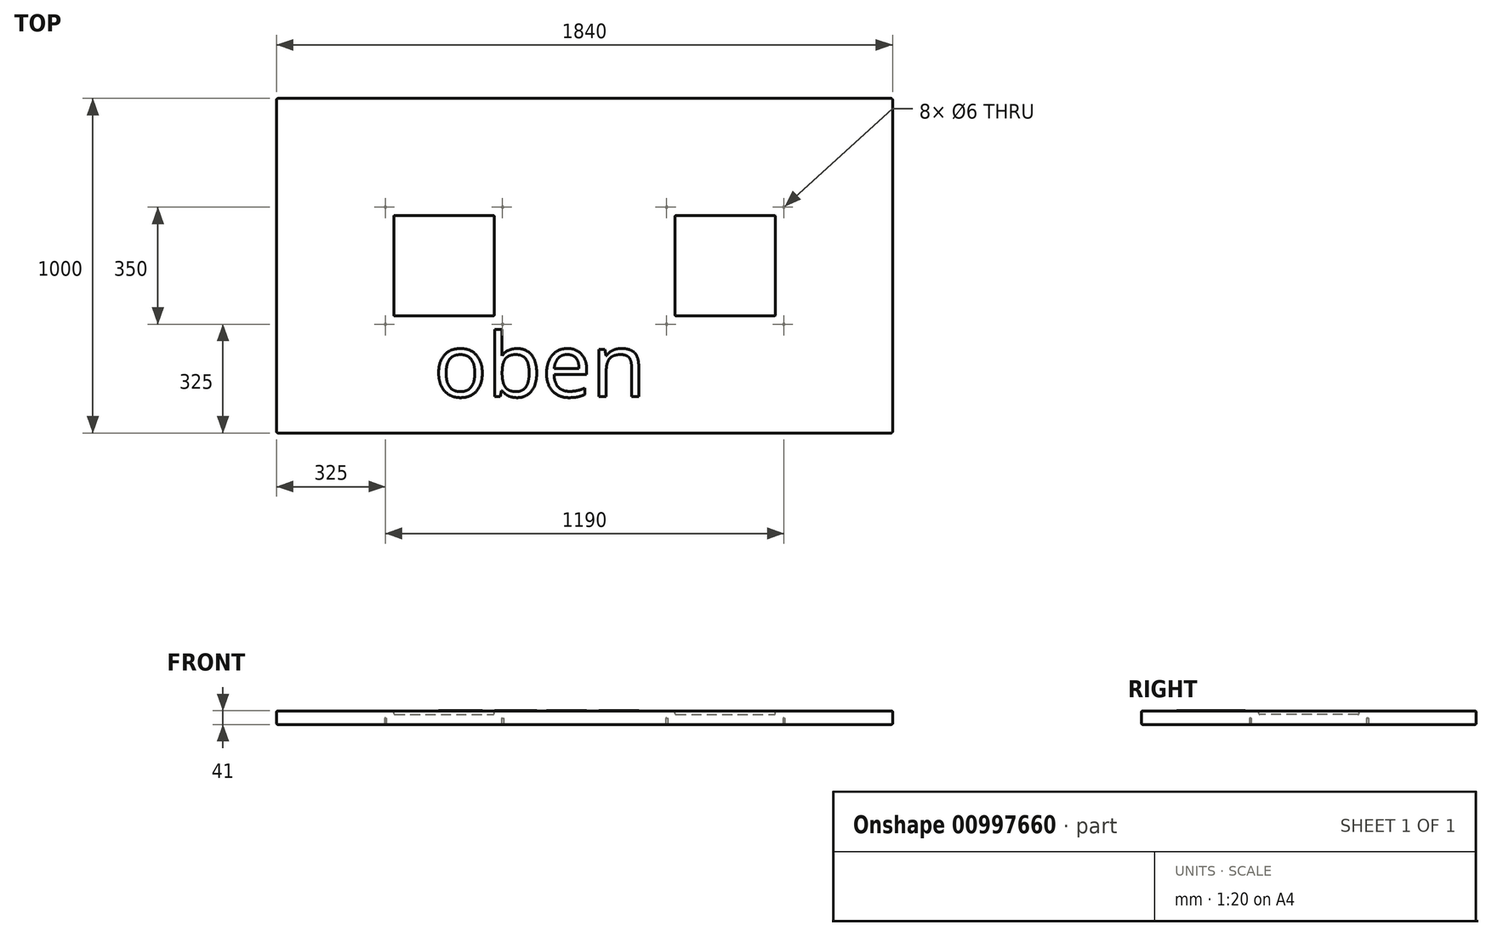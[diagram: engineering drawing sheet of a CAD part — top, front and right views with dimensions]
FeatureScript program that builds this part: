
annotation { "Feature Type Name" : "Feature", "Feature Type Description" : "" }
export const myFeature = defineFeature(function(context is Context, id is Id, definition is map)
    precondition{}
    {
        {
            var Q0;
            Q0=qCreatedBy(makeId("Top.planeOp"),FACE);
            var sketch = newSketch(context, id + "F0", { "sketchPlane" : qUnion([Q0])});
            skLineSegment(sketch, "E0.bottom", {"start": v(0, 0) * mm, "end": v(1840, 0) * mm});
            skLineSegment(sketch, "E0.top", {"start": v(0, 1000) * mm, "end": v(1840, 1000) * mm});
            skLineSegment(sketch, "E0.left", {"start": v(0, 0) * mm, "end": v(0, 1000) * mm});
            skLineSegment(sketch, "E0.right", {"start": v(1840, 0) * mm, "end": v(1840, 1000) * mm});
            skSolve(sketch);
        }
        {
            var Q0;
            Q0=makeQuery(id+"F0.imprint","IMPRINT",FACE,{"disambiguationData":[TD([[makeQuery(id+"F0.imprint","IMPRINT",EDGE,{"derivedFrom":sQuery(id+"F0.wireOp",EDGE,"E0.bottom")}),1.0]])]});
            extrude(context, id + "F1", {"entities" : qUnion([Q0]), "depth" : 40 * mm, "offsetDistance" : 25 * mm});
        }
        {
            var Q0;
            Q0=makeQuery(id+"F1.opExtrude","CAP_FACE",FACE,{"disambiguationData":[OSD([sQuery(id+"F0.wireOp",EDGE,"E0.bottom"),sQuery(id+"F0.wireOp",EDGE,"E0.top"),sQuery(id+"F0.wireOp",EDGE,"E0.left"),sQuery(id+"F0.wireOp",EDGE,"E0.right")])],"isStart":false});
            var sketch = newSketch(context, id + "F2", { "sketchPlane" : qUnion([Q0])});
            skLineSegment(sketch, "E1.bottom", {"start": v(350, 650) * mm, "end": v(650, 650) * mm});
            skLineSegment(sketch, "E1.top", {"start": v(350, 350) * mm, "end": v(650, 350) * mm});
            skLineSegment(sketch, "E1.left", {"start": v(350, 650) * mm, "end": v(350, 350) * mm});
            skLineSegment(sketch, "E1.right", {"start": v(650, 650) * mm, "end": v(650, 350) * mm});
            skLineSegment(sketch, "E2.bottom", {"start": v(1190, 650) * mm, "end": v(1490, 650) * mm});
            skLineSegment(sketch, "E2.top", {"start": v(1190, 350) * mm, "end": v(1490, 350) * mm});
            skLineSegment(sketch, "E2.left", {"start": v(1190, 650) * mm, "end": v(1190, 350) * mm});
            skLineSegment(sketch, "E2.right", {"start": v(1490, 650) * mm, "end": v(1490, 350) * mm});
            skSolve(sketch);
        }
        {
            var Q0;
            Q0=makeQuery(id+"F2.imprint","IMPRINT",FACE,{"disambiguationData":[TD([[makeQuery(id+"F2.imprint","IMPRINT",EDGE,{"derivedFrom":sQuery(id+"F2.wireOp",EDGE,"E2.bottom")}),-1.0]])]});
            var Q1;
            Q1=makeQuery(id+"F2.imprint","IMPRINT",FACE,{"disambiguationData":[TD([[makeQuery(id+"F2.imprint","IMPRINT",EDGE,{"derivedFrom":sQuery(id+"F2.wireOp",EDGE,"E1.bottom")}),-1.0]])]});
            extrude(context, id + "F3", {"entities" : qUnion([Q0, Q1]), "operationType" : NewBodyOperationType.REMOVE, "oppositeDirection" : true, "depth" : 10 * mm, "offsetDistance" : 25 * mm});
        }
        {
            var Q0;
            Q0=makeQuery(id+"F3.boolean.opBoolean","COPY",EDGE,{"derivedFrom":makeQuery(id+"F3.opExtrude","SWEPT_EDGE",EDGE,{"disambiguationData":[OSD([sQuery(id+"F2.wireOp",EDGE,"E2.bottom"),sQuery(id+"F2.wireOp",EDGE,"E2.right")])]})});
            var Q1;
            Q1=makeQuery(id+"F3.boolean.opBoolean","COPY",EDGE,{"derivedFrom":makeQuery(id+"F3.opExtrude","SWEPT_EDGE",EDGE,{"disambiguationData":[OSD([sQuery(id+"F2.wireOp",EDGE,"E2.bottom"),sQuery(id+"F2.wireOp",EDGE,"E2.left")])]})});
            var Q2;
            Q2=makeQuery(id+"F3.boolean.opBoolean","COPY",EDGE,{"derivedFrom":makeQuery(id+"F3.opExtrude","SWEPT_EDGE",EDGE,{"disambiguationData":[OSD([sQuery(id+"F2.wireOp",EDGE,"E2.top"),sQuery(id+"F2.wireOp",EDGE,"E2.left")])]})});
            var Q3;
            Q3=makeQuery(id+"F3.boolean.opBoolean","COPY",EDGE,{"derivedFrom":makeQuery(id+"F3.opExtrude","SWEPT_EDGE",EDGE,{"disambiguationData":[OSD([sQuery(id+"F2.wireOp",EDGE,"E2.top"),sQuery(id+"F2.wireOp",EDGE,"E2.right")])]})});
            var Q4;
            Q4=makeQuery(id+"F3.boolean.opBoolean","COPY",EDGE,{"derivedFrom":makeQuery(id+"F3.opExtrude","SWEPT_EDGE",EDGE,{"disambiguationData":[OSD([sQuery(id+"F2.wireOp",EDGE,"E1.bottom"),sQuery(id+"F2.wireOp",EDGE,"E1.right")])]})});
            var Q5;
            Q5=makeQuery(id+"F3.boolean.opBoolean","COPY",EDGE,{"derivedFrom":makeQuery(id+"F3.opExtrude","SWEPT_EDGE",EDGE,{"disambiguationData":[OSD([sQuery(id+"F2.wireOp",EDGE,"E1.bottom"),sQuery(id+"F2.wireOp",EDGE,"E1.left")])]})});
            var Q6;
            Q6=makeQuery(id+"F3.boolean.opBoolean","COPY",EDGE,{"derivedFrom":makeQuery(id+"F3.opExtrude","SWEPT_EDGE",EDGE,{"disambiguationData":[OSD([sQuery(id+"F2.wireOp",EDGE,"E1.top"),sQuery(id+"F2.wireOp",EDGE,"E1.left")])]})});
            var Q7;
            Q7=makeQuery(id+"F3.boolean.opBoolean","COPY",EDGE,{"derivedFrom":makeQuery(id+"F3.opExtrude","SWEPT_EDGE",EDGE,{"disambiguationData":[OSD([sQuery(id+"F2.wireOp",EDGE,"E1.top"),sQuery(id+"F2.wireOp",EDGE,"E1.right")])]})});
            var Q8;
            Q8=makeQuery(id+"F3.boolean.opBoolean","COPY",FACE,{"derivedFrom":makeQuery(id+"F3.opExtrude","CAP_FACE",FACE,{"disambiguationData":[OSD([sQuery(id+"F2.wireOp",EDGE,"E2.bottom"),sQuery(id+"F2.wireOp",EDGE,"E2.top"),sQuery(id+"F2.wireOp",EDGE,"E2.left"),sQuery(id+"F2.wireOp",EDGE,"E2.right")])],"isStart":false})});
            var Q9;
            Q9=makeQuery(id+"F3.boolean.opBoolean","COPY",EDGE,{"derivedFrom":makeQuery(id+"F3.opExtrude","CAP_EDGE",EDGE,{"disambiguationData":[OSD([sQuery(id+"F2.wireOp",EDGE,"E1.right")])],"isStart":false})});
            var Q10;
            Q10=makeQuery(id+"F3.boolean.opBoolean","COPY",EDGE,{"derivedFrom":makeQuery(id+"F3.opExtrude","CAP_EDGE",EDGE,{"disambiguationData":[OSD([sQuery(id+"F2.wireOp",EDGE,"E1.bottom")])],"isStart":false})});
            var Q11;
            Q11=makeQuery(id+"F3.boolean.opBoolean","COPY",EDGE,{"derivedFrom":makeQuery(id+"F3.opExtrude","CAP_EDGE",EDGE,{"disambiguationData":[OSD([sQuery(id+"F2.wireOp",EDGE,"E1.left")])],"isStart":false})});
            var Q12;
            Q12=makeQuery(id+"F3.boolean.opBoolean","COPY",EDGE,{"derivedFrom":makeQuery(id+"F3.opExtrude","CAP_EDGE",EDGE,{"disambiguationData":[OSD([sQuery(id+"F2.wireOp",EDGE,"E1.top")])],"isStart":false})});
            var Q13;
            Q13=makeQuery(id+"F1.opExtrude","CAP_EDGE",EDGE,{"disambiguationData":[OSD([sQuery(id+"F0.wireOp",EDGE,"E0.left")])],"isStart":false});
            var Q14;
            Q14=makeQuery(id+"F1.opExtrude","CAP_EDGE",EDGE,{"disambiguationData":[OSD([sQuery(id+"F0.wireOp",EDGE,"E0.bottom")])],"isStart":false});
            var Q15;
            Q15=makeQuery(id+"F1.opExtrude","CAP_EDGE",EDGE,{"disambiguationData":[OSD([sQuery(id+"F0.wireOp",EDGE,"E0.right")])],"isStart":false});
            var Q16;
            Q16=makeQuery(id+"F1.opExtrude","CAP_EDGE",EDGE,{"disambiguationData":[OSD([sQuery(id+"F0.wireOp",EDGE,"E0.top")])],"isStart":false});
            var Q17;
            Q17=makeQuery(id+"F1.opExtrude","CAP_FACE",FACE,{"disambiguationData":[OSD([sQuery(id+"F0.wireOp",EDGE,"E0.bottom"),sQuery(id+"F0.wireOp",EDGE,"E0.top"),sQuery(id+"F0.wireOp",EDGE,"E0.left"),sQuery(id+"F0.wireOp",EDGE,"E0.right")])],"isStart":true});
            fillet(context, id + "F4", {"entities" : qUnion([Q0, Q1, Q2, Q3, Q4, Q5, Q6, Q7, Q8, Q9, Q10, Q11, Q12, Q13, Q14, Q15, Q16, Q17]), "tangentPropagation" : true, "radius" : 3 * mm, "defaultsChanged" : false, "vertexSettings" : [], "allowEdgeOverflow" : false});
        }
        {
            var Q0;
            Q0=makeQuery(id+"F1.opExtrude","CAP_FACE",FACE,{"disambiguationData":[OSD([sQuery(id+"F0.wireOp",EDGE,"E0.bottom"),sQuery(id+"F0.wireOp",EDGE,"E0.top"),sQuery(id+"F0.wireOp",EDGE,"E0.left"),sQuery(id+"F0.wireOp",EDGE,"E0.right")])],"isStart":false});
            var sketch = newSketch(context, id + "F5", { "sketchPlane" : qUnion([Q0])});
            skText(sketch, "E3", { "text": "oben", "fontName": "OpenSans-Regular.ttf"});
            const initialGuessF5  = {"E3": [0.46929, 0.10821, 1, 0, 0.19075]};
            skSetInitialGuess(sketch, initialGuessF5);
            skSolve(sketch);
        }
        {
            var Q0;
            Q0=makeQuery(id+"F1.opExtrude","SWEPT_EDGE",EDGE,{"disambiguationData":[OSD([sQuery(id+"F0.wireOp",EDGE,"E0.top"),sQuery(id+"F0.wireOp",EDGE,"E0.right")])]});
            var Q1;
            Q1=makeQuery(id+"F1.opExtrude","SWEPT_EDGE",EDGE,{"disambiguationData":[OSD([sQuery(id+"F0.wireOp",EDGE,"E0.bottom"),sQuery(id+"F0.wireOp",EDGE,"E0.right")])]});
            var Q2;
            Q2=makeQuery(id+"F1.opExtrude","SWEPT_EDGE",EDGE,{"disambiguationData":[OSD([sQuery(id+"F0.wireOp",EDGE,"E0.bottom"),sQuery(id+"F0.wireOp",EDGE,"E0.left")])]});
            var Q3;
            Q3=makeQuery(id+"F1.opExtrude","SWEPT_EDGE",EDGE,{"disambiguationData":[OSD([sQuery(id+"F0.wireOp",EDGE,"E0.top"),sQuery(id+"F0.wireOp",EDGE,"E0.left")])]});
            fillet(context, id + "F6", {"entities" : qUnion([Q0, Q1, Q2, Q3]), "tangentPropagation" : true, "radius" : 5 * mm, "defaultsChanged" : false, "vertexSettings" : [], "allowEdgeOverflow" : false});
        }
        {
            var Q0;
            Q0=makeQuery(id+"F1.opExtrude","CAP_FACE",FACE,{"disambiguationData":[OSD([sQuery(id+"F0.wireOp",EDGE,"E0.bottom"),sQuery(id+"F0.wireOp",EDGE,"E0.top"),sQuery(id+"F0.wireOp",EDGE,"E0.left"),sQuery(id+"F0.wireOp",EDGE,"E0.right")])],"isStart":true});
            var sketch = newSketch(context, id + "F7", { "sketchPlane" : qUnion([Q0])});
            skLineSegment(sketch, "E4.bottom", {"start": v(325, -325) * mm, "end": v(675, -325) * mm, "construction": true});
            skLineSegment(sketch, "E4.top", {"start": v(325, -675) * mm, "end": v(675, -675) * mm, "construction": true});
            skLineSegment(sketch, "E4.left", {"start": v(325, -325) * mm, "end": v(325, -675) * mm, "construction": true});
            skLineSegment(sketch, "E4.right", {"start": v(675, -325) * mm, "end": v(675, -675) * mm, "construction": true});
            skLineSegment(sketch, "E5.bottom", {"start": v(400, -400) * mm, "end": v(600, -400) * mm, "construction": true});
            skLineSegment(sketch, "E5.top", {"start": v(400, -600) * mm, "end": v(600, -600) * mm, "construction": true});
            skLineSegment(sketch, "E5.left", {"start": v(400, -400) * mm, "end": v(400, -600) * mm, "construction": true});
            skLineSegment(sketch, "E5.right", {"start": v(600, -400) * mm, "end": v(600, -600) * mm, "construction": true});
            skLineSegment(sketch, "E6.1.0.0", {"start": v(1165, -325) * mm, "end": v(1515, -325) * mm, "construction": true});
            skLineSegment(sketch, "E6.1.0.1", {"start": v(1165, -325) * mm, "end": v(1165, -675) * mm, "construction": true});
            skLineSegment(sketch, "E6.1.0.2", {"start": v(1240, -400) * mm, "end": v(1240, -600) * mm, "construction": true});
            skLineSegment(sketch, "E6.1.0.3", {"start": v(1240, -400) * mm, "end": v(1440, -400) * mm, "construction": true});
            skLineSegment(sketch, "E6.1.0.4", {"start": v(1440, -400) * mm, "end": v(1440, -600) * mm, "construction": true});
            skLineSegment(sketch, "E6.1.0.5", {"start": v(1240, -600) * mm, "end": v(1440, -600) * mm, "construction": true});
            skLineSegment(sketch, "E6.1.0.6", {"start": v(1515, -325) * mm, "end": v(1515, -675) * mm, "construction": true});
            skLineSegment(sketch, "E6.1.0.7", {"start": v(1165, -675) * mm, "end": v(1515, -675) * mm, "construction": true});
            skLineSegment(sketch, "E6.direction1", {"start": v(325, -675) * mm, "end": v(1165, -675) * mm, "construction": true});
            skSolve(sketch);
        }
        {
            var Q0;
            Q0=sQuery(id+"F7.wireOp",VERTEX,"E4.bottom.start");
            var Q1;
            Q1=sQuery(id+"F7.wireOp",VERTEX,"E4.bottom.end");
            var Q2;
            Q2=sQuery(id+"F7.wireOp",VERTEX,"E4.top.start");
            var Q3;
            Q3=sQuery(id+"F7.wireOp",VERTEX,"E4.top.end");
            var Q4;
            Q4=sQuery(id+"F7.wireOp",VERTEX,"E6.1.0.1.end");
            var Q5;
            Q5=sQuery(id+"F7.wireOp",VERTEX,"E6.1.0.0.start");
            var Q6;
            Q6=sQuery(id+"F7.wireOp",VERTEX,"E6.1.0.0.end");
            var Q7;
            Q7=sQuery(id+"F7.wireOp",VERTEX,"E6.1.0.6.end");
            var Q8;
            Q8=makeQuery(id+"F1.opExtrude","SWEPT_BODY",BODY,{"disambiguationData":[OSD([sQuery(id+"F0.wireOp",EDGE,"E0.bottom"),sQuery(id+"F0.wireOp",EDGE,"E0.top"),sQuery(id+"F0.wireOp",EDGE,"E0.left"),sQuery(id+"F0.wireOp",EDGE,"E0.right")])]});
            hole(context, id + "F8", {"style" : HoleStyle.SIMPLE, "endStyle" : HoleEndStyle.BLIND, "holeDiameter" : 6 * mm, "majorDiameter" : 5 * mm, "holeDepth" : 18 * mm, "isTappedThrough" : true, "tappedDepth" : 12 * mm, "tapClearance" : 3, "locations" : qUnion([Q0, Q1, Q2, Q3, Q4, Q5, Q6, Q7]), "scope" : qUnion([Q8])});
        }
        {
            var Q0;
            Q0 = qSketchRegion(id + "F5", true);
            extrude(context, id + "F9", {"entities" : qUnion([Q0]), "operationType" : NewBodyOperationType.ADD, "depth" : 1 * mm, "offsetDistance" : 25 * mm});
        }
    });
